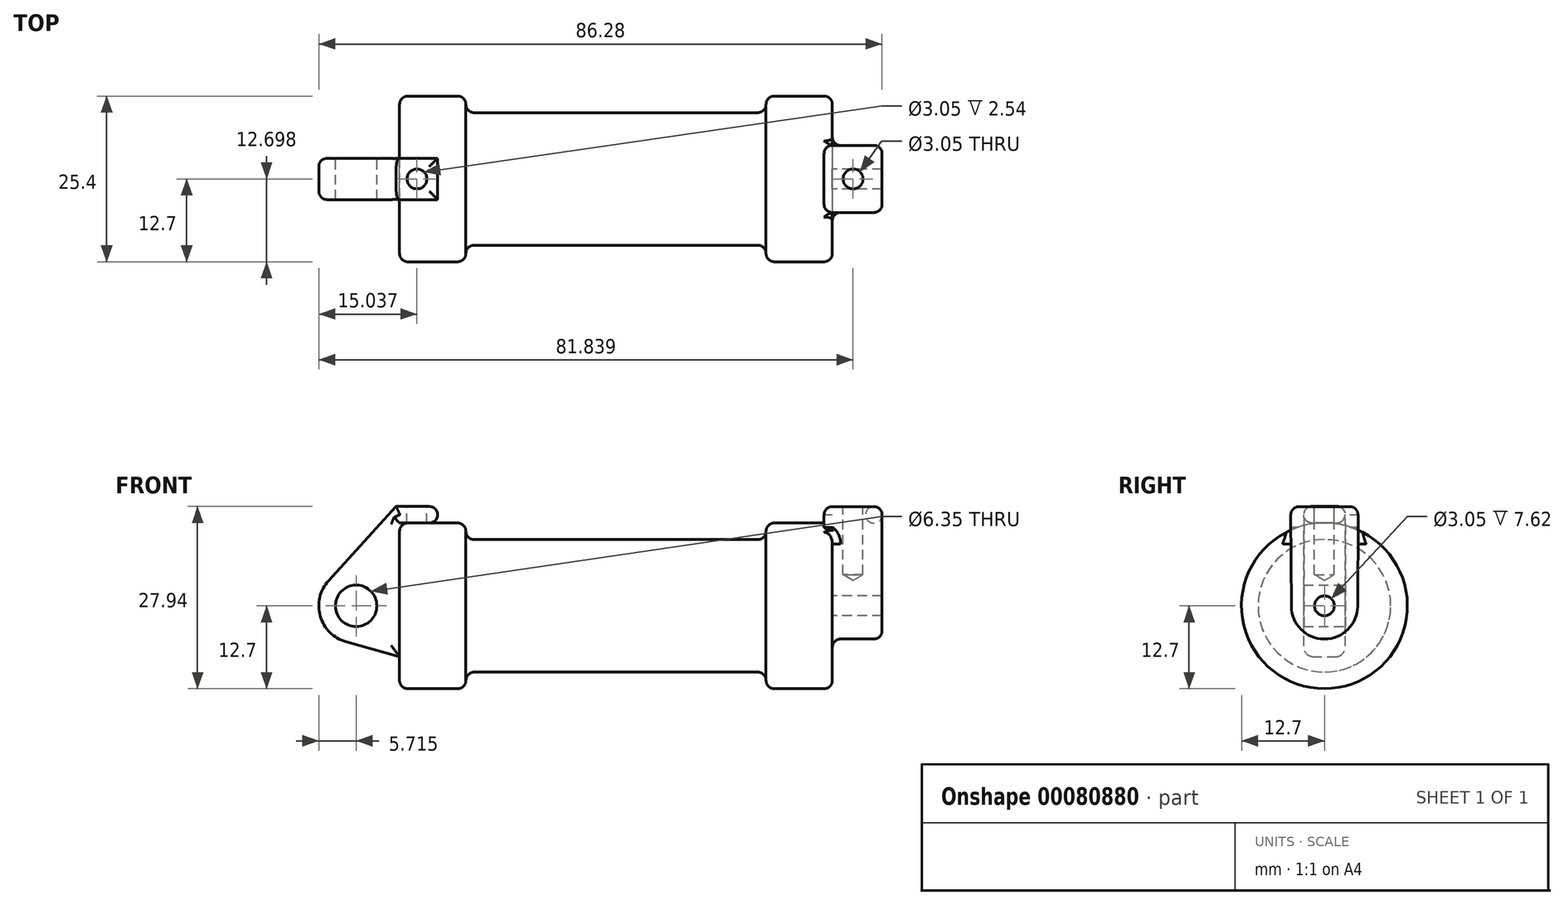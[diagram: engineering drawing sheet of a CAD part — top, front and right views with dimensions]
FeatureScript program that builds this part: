
annotation { "Feature Type Name" : "Feature", "Feature Type Description" : "" }
export const myFeature = defineFeature(function(context is Context, id is Id, definition is map)
    precondition{}
    {
        {
            var Q0;
            Q0=qCreatedBy(makeId("Front.planeOp"),FACE);
            var sketch = newSketch(context, id + "F0", { "sketchPlane" : qUnion([Q0])});
            skLineSegment(sketch, "E0", {"start": v(0, 0) * mm, "end": v(0, 12.7) * mm});
            skLineSegment(sketch, "E1", {"start": v(0, 12.7) * mm, "end": v(10.16, 12.7) * mm});
            skLineSegment(sketch, "E2", {"start": v(10.16, 12.7) * mm, "end": v(10.16, 10.16) * mm});
            skLineSegment(sketch, "E3", {"start": v(10.16, 10.16) * mm, "end": v(56.13, 10.16) * mm});
            skLineSegment(sketch, "E4", {"start": v(56.13, 10.16) * mm, "end": v(56.13, 12.7) * mm});
            skLineSegment(sketch, "E5", {"start": v(56.13, 12.7) * mm, "end": v(66.3, 12.7) * mm});
            skLineSegment(sketch, "E6", {"start": v(66.3, 12.7) * mm, "end": v(66.3, 0) * mm});
            skLineSegment(sketch, "E7", {"start": v(66.3, 0) * mm, "end": v(0, 0) * mm});
            skLineSegment(sketch, "E8", {"start": v(5.84, 15.24) * mm, "end": v(-0.5, 15.24) * mm});
            skLineSegment(sketch, "E9", {"start": v(-0.5, 15.24) * mm, "end": v(-10.88, 3.85) * mm});
            skLineSegment(sketch, "E10", {"start": v(0, 0) * mm, "end": v(-6.65, 0) * mm});
            skCircle(sketch, "E11", {"center": v(-6.65, 0) * mm, "radius": 5.72 * mm});
            skCircle(sketch, "E12", {"center": v(-6.65, 0) * mm, "radius": 3.18 * mm});
            skLineSegment(sketch, "E13", {"start": v(5.84, 15.24) * mm, "end": v(5.84, -9.4) * mm});
            skLineSegment(sketch, "E14", {"start": v(5.84, -9.4) * mm, "end": v(-8.18, -5.5) * mm});
            skLineSegment(sketch, "E15", {"start": v(5.84, 0) * mm, "end": v(66.3, 0) * mm});
            skLineSegment(sketch, "E16", {"start": v(5.84, 0) * mm, "end": v(5.84, 0) * mm});
            skLineSegment(sketch, "E17", {"start": v(0, 0) * mm, "end": v(0, -7.78) * mm});
            skSolve(sketch);
        }
        {
            var Q0;
            {var subQ0=sQuery(id+"F0.wireOp",EDGE,"E2");Q0=makeQuery(id+"F0.imprint","IMPRINT",FACE,{"disambiguationData":[TD([[makeQuery(id+"F0.imprint","IMPRINT",EDGE,{"derivedFrom":subQ0}),-1.0]])]});}
            var Q1;
            {var subQ0=sQuery(id+"F0.wireOp",EDGE,"E0");Q1=makeQuery(id+"F0.imprint","IMPRINT",FACE,{"disambiguationData":[TD([[makeQuery(id+"F0.imprint","IMPRINT",EDGE,{"derivedFrom":subQ0}),-1.0]])]});}
            var Q2;
            Q2=sQuery(id+"F0.wireOp",EDGE,"E7");
            revolve(context, id + "F1", {"entities" : qUnion([Q0, Q1]), "axis" : qUnion([Q2]), "revolveType" : RevolveType.FULL});
        }
        {
            var Q0;
            {var subQ3=sQuery(id+"F0.wireOp",EDGE,"E0");Q0=makeQuery(id+"F0.imprint","IMPRINT",FACE,{"disambiguationData":[TD([[makeQuery(id+"F0.imprint","IMPRINT",EDGE,{"derivedFrom":subQ3}),1.0]])]});}
            var Q1;
            {var subQ0=sQuery(id+"F0.wireOp",EDGE,"E17");Q1=makeQuery(id+"F0.imprint","IMPRINT",FACE,{"disambiguationData":[TD([[makeQuery(id+"F0.imprint","IMPRINT",EDGE,{"derivedFrom":subQ0}),-1.0]])]});}
            var Q2;
            {var subQ4=sQuery(id+"F0.wireOp",EDGE,"E12");Q2=makeQuery(id+"F0.imprint","IMPRINT",FACE,{"disambiguationData":[TD([[makeQuery(id+"F0.imprint","IMPRINT",EDGE,{"derivedFrom":subQ4}),-1.0]])]});}
            extrude(context, id + "F2", {"entities" : qUnion([Q0, Q1, Q2]), "endBound" : BoundingType.SYMMETRIC, "depth" : 6.35 * mm});
        }
        {
            var Q0;
            Q0=makeQuery(id+"F1.opRevolve","SWEPT_FACE",FACE,{"disambiguationData":[OSD([sQuery(id+"F0.wireOp",EDGE,"E6")])]});
            var sketch = newSketch(context, id + "F3", { "sketchPlane" : qUnion([Q0])});
            skCircle(sketch, "E18", {"center": v(0, 0) * mm, "radius": 1.52 * mm});
            skCircle(sketch, "E19", {"center": v(0, 0) * mm, "radius": 5.08 * mm});
            skLineSegment(sketch, "E20", {"start": v(-5.16, 15.21) * mm, "end": v(5.15, 15.22) * mm});
            skLineSegment(sketch, "E21", {"start": v(-5.16, 15.21) * mm, "end": v(-5.08, -0.03) * mm});
            skLineSegment(sketch, "E22", {"start": v(5.15, 15.22) * mm, "end": v(5.08, -0.02) * mm});
            skSolve(sketch);
        }
        {
            var Q0;
            Q0 = qSketchRegion(id + "F3", true);
            extrude(context, id + "F4", {"entities" : qUnion([Q0]), "operationType" : NewBodyOperationType.ADD, "depth" : 7.62 * mm, "hasSecondDirection" : true, "secondDirectionOppositeDirection" : true, "secondDirectionDepth" : 1.27 * mm});
        }
        {
            var Q0;
            Q0=makeQuery(id+"F2.opExtrude","SWEPT_FACE",FACE,{"disambiguationData":[OSD([sQuery(id+"F0.wireOp",EDGE,"E8")])]});
            var sketch = newSketch(context, id + "F5", { "sketchPlane" : qUnion([Q0])});
            skLineSegment(sketch, "E23", {"start": v(2.67, 3.18) * mm, "end": v(2.67, -3.18) * mm});
            skPoint(sketch, "E24", {"position": v(2.67, 0) * mm});
            skSolve(sketch);
        }
        {
            var Q0;
            Q0=makeQuery(id+"F4.opExtrude","SWEPT_FACE",FACE,{"disambiguationData":[OSD([sQuery(id+"F3.wireOp",EDGE,"E20")])]});
            var sketch = newSketch(context, id + "F6", { "sketchPlane" : qUnion([Q0])});
            skLineSegment(sketch, "E25", {"start": v(65.02, 0) * mm, "end": v(73.91, 0) * mm});
            skPoint(sketch, "E26", {"position": v(69.47, 0) * mm});
            skSolve(sketch);
        }
        {
            var Q0;
            Q0=sQuery(id+"F5.wireOp",VERTEX,"E24");
            var Q1;
            Q1=makeQuery(id+"F2.opExtrude","SWEPT_BODY",BODY,{"disambiguationData":[OSD([sQuery(id+"F0.wireOp",EDGE,"E0"),sQuery(id+"F0.wireOp",EDGE,"E1"),sQuery(id+"F0.wireOp",EDGE,"E8"),sQuery(id+"F0.wireOp",EDGE,"E9"),sQuery(id+"F0.wireOp",EDGE,"E11"),sQuery(id+"F0.wireOp",EDGE,"E12"),sQuery(id+"F0.wireOp",EDGE,"E13"),sQuery(id+"F0.wireOp",EDGE,"E14"),sQuery(id+"F0.wireOp",EDGE,"E17")])]});
            hole(context, id + "F7", {"style" : HoleStyle.SIMPLE, "endStyle" : HoleEndStyle.BLIND, "holeDiameter" : 3.05 * mm, "holeDepth" : 17.78 * mm, "locations" : qUnion([Q0]), "scope" : qUnion([Q1])});
        }
        {
            var Q0;
            Q0=sQuery(id+"F6.wireOp",VERTEX,"E26");
            var Q1;
            Q1=makeQuery(id+"F1.opRevolve","SWEPT_BODY",BODY,{"disambiguationData":[OSD([sQuery(id+"F0.wireOp",EDGE,"E0"),sQuery(id+"F0.wireOp",EDGE,"E1"),sQuery(id+"F0.wireOp",EDGE,"E2"),sQuery(id+"F0.wireOp",EDGE,"E3"),sQuery(id+"F0.wireOp",EDGE,"E4"),sQuery(id+"F0.wireOp",EDGE,"E5"),sQuery(id+"F0.wireOp",EDGE,"E6"),sQuery(id+"F0.wireOp",EDGE,"E7"),sQuery(id+"F0.wireOp",EDGE,"E15")])]});
            hole(context, id + "F8", {"style" : HoleStyle.SIMPLE, "endStyle" : HoleEndStyle.BLIND, "holeDiameter" : 3.05 * mm, "holeDepth" : 10.4 * mm, "startFromSketch" : true, "locations" : qUnion([Q0]), "scope" : qUnion([Q1])});
        }
        {
            var Q0;
            Q0=makeQuery(id+"F1.opRevolve","SWEPT_FACE",FACE,{"disambiguationData":[OSD([sQuery(id+"F0.wireOp",EDGE,"E2")])]});
            var Q1;
            Q1=makeQuery(id+"F1.opRevolve","SWEPT_FACE",FACE,{"disambiguationData":[OSD([sQuery(id+"F0.wireOp",EDGE,"E4")])]});
            var Q2;
            Q2=makeQuery(id+"F4.boolean.opBoolean","SPLIT",FACE,{"disambiguationData":[TD([makeQuery(id+"F1.opRevolve","SWEPT_FACE",FACE,{"disambiguationData":[OSD([sQuery(id+"F0.wireOp",EDGE,"E5")])]})])],"derivedFrom":makeQuery(id+"F1.opRevolve","SWEPT_FACE",FACE,{"disambiguationData":[OSD([sQuery(id+"F0.wireOp",EDGE,"E6")])]})});
            var Q3;
            Q3=makeQuery(id+"F1.opRevolve","SWEPT_FACE",FACE,{"disambiguationData":[OSD([sQuery(id+"F0.wireOp",EDGE,"E0")])]});
            fillet(context, id + "F9", {"entities" : qUnion([Q0, Q1, Q2, Q3]), "radius" : 1.27 * mm, "tangentPropagation" : true, "allowEdgeOverflow" : false});
        }
        {
            var Q0;
            Q0=makeQuery(id+"F2.opExtrude","CAP_EDGE",EDGE,{"disambiguationData":[OSD([sQuery(id+"F0.wireOp",EDGE,"E8")])],"isStart":false});
            var Q1;
            Q1=makeQuery(id+"F2.opExtrude","CAP_EDGE",EDGE,{"disambiguationData":[OSD([sQuery(id+"F0.wireOp",EDGE,"E1")])],"isStart":false});
            var Q2;
            Q2=makeQuery(id+"F2.opExtrude","SWEPT_EDGE",EDGE,{"disambiguationData":[OSD([sQuery(id+"F0.wireOp",EDGE,"E1"),sQuery(id+"F0.wireOp",EDGE,"E13")])]});
            var Q3;
            Q3=makeQuery(id+"F2.opExtrude","SWEPT_EDGE",EDGE,{"disambiguationData":[OSD([sQuery(id+"F0.wireOp",EDGE,"E8"),sQuery(id+"F0.wireOp",EDGE,"E13")])]});
            var Q4;
            Q4=makeQuery(id+"F2.opExtrude","CAP_EDGE",EDGE,{"disambiguationData":[OSD([sQuery(id+"F0.wireOp",EDGE,"E1")])],"isStart":true});
            var Q5;
            Q5=makeQuery(id+"F2.opExtrude","CAP_EDGE",EDGE,{"disambiguationData":[OSD([sQuery(id+"F0.wireOp",EDGE,"E8")])],"isStart":true});
            var Q6;
            Q6=makeQuery(id+"F2.opExtrude","CAP_EDGE",EDGE,{"disambiguationData":[OSD([sQuery(id+"F0.wireOp",EDGE,"E0"),sQuery(id+"F0.wireOp",EDGE,"E17")])],"isStart":true});
            var Q7;
            Q7=makeQuery(id+"F2.opExtrude","CAP_EDGE",EDGE,{"disambiguationData":[OSD([sQuery(id+"F0.wireOp",EDGE,"E9")])],"isStart":true});
            var Q8;
            Q8=makeQuery(id+"F2.opExtrude","CAP_EDGE",EDGE,{"disambiguationData":[OSD([sQuery(id+"F0.wireOp",EDGE,"E9")])],"isStart":false});
            var Q9;
            Q9=makeQuery(id+"F2.opExtrude","CAP_EDGE",EDGE,{"disambiguationData":[OSD([sQuery(id+"F0.wireOp",EDGE,"E11")])],"isStart":false});
            var Q10;
            Q10=makeQuery(id+"F2.opExtrude","CAP_EDGE",EDGE,{"disambiguationData":[OSD([sQuery(id+"F0.wireOp",EDGE,"E14")])],"isStart":false});
            var Q11;
            Q11=makeQuery(id+"F2.opExtrude","CAP_EDGE",EDGE,{"disambiguationData":[OSD([sQuery(id+"F0.wireOp",EDGE,"E0"),sQuery(id+"F0.wireOp",EDGE,"E17")])],"isStart":false});
            fillet(context, id + "F10", {"entities" : qUnion([Q0, Q1, Q2, Q3, Q4, Q5, Q6, Q7, Q8, Q9, Q10, Q11]), "radius" : 1.27 * mm, "tangentPropagation" : true, "allowEdgeOverflow" : false});
        }
        {
            var Q0;
            Q0=makeQuery(id+"F4.opExtrude","CAP_EDGE",EDGE,{"disambiguationData":[OSD([sQuery(id+"F3.wireOp",EDGE,"E22")])],"isStart":false});
            var Q1;
            Q1=makeQuery(id+"F4.opExtrude","SWEPT_EDGE",EDGE,{"disambiguationData":[OSD([sQuery(id+"F3.wireOp",EDGE,"E20"),sQuery(id+"F3.wireOp",EDGE,"E22")])]});
            var Q2;
            Q2=makeQuery(id+"F4.opExtrude","CAP_EDGE",EDGE,{"disambiguationData":[OSD([sQuery(id+"F3.wireOp",EDGE,"E20")])],"isStart":false});
            var Q3;
            Q3=makeQuery(id+"F4.opExtrude","SWEPT_EDGE",EDGE,{"disambiguationData":[OSD([sQuery(id+"F3.wireOp",EDGE,"E20"),sQuery(id+"F3.wireOp",EDGE,"E21")])]});
            var Q4;
            Q4=makeQuery(id+"F4.opExtrude","CAP_EDGE",EDGE,{"disambiguationData":[OSD([sQuery(id+"F3.wireOp",EDGE,"E20")])],"isStart":true});
            var Q5;
            Q5=makeQuery(id+"F4.opExtrude","CAP_EDGE",EDGE,{"disambiguationData":[OSD([sQuery(id+"F3.wireOp",EDGE,"E22")])],"isStart":true});
            fillet(context, id + "F11", {"entities" : qUnion([Q0, Q1, Q2, Q3, Q4, Q5]), "radius" : 1.27 * mm, "tangentPropagation" : true, "allowEdgeOverflow" : false});
        }
    });
